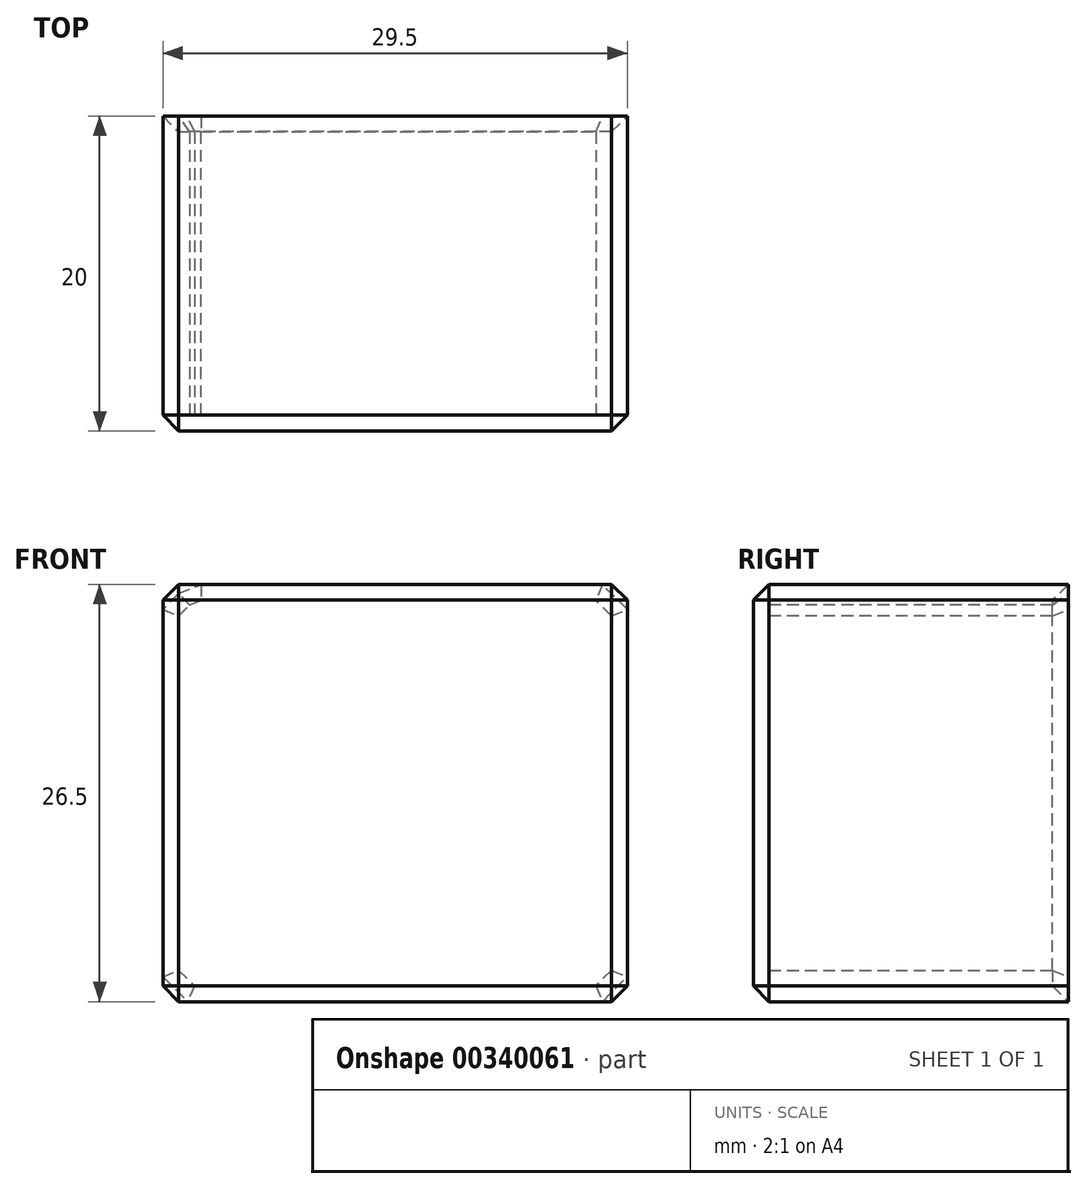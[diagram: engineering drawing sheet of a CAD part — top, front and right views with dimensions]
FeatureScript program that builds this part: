
annotation { "Feature Type Name" : "Feature", "Feature Type Description" : "" }
export const myFeature = defineFeature(function(context is Context, id is Id, definition is map)
    precondition{}
    {
        {
            var Q0;
            Q0=qCreatedBy(makeId("Front.planeOp"),FACE);
            var sketch = newSketch(context, id + "F0", { "sketchPlane" : qUnion([Q0])});
            skLineSegment(sketch, "E0.bottom", {"start": v(0, 0) * mm, "end": v(27.5, 0) * mm});
            skLineSegment(sketch, "E0.top", {"start": v(0, -24.5) * mm, "end": v(27.5, -24.5) * mm});
            skLineSegment(sketch, "E0.left", {"start": v(0, 0) * mm, "end": v(0, -24.5) * mm});
            skLineSegment(sketch, "E0.right", {"start": v(27.5, 0) * mm, "end": v(27.5, -24.5) * mm});
            skLineSegment(sketch, "E1", {"start": v(-1, 1) * mm, "end": v(-1, -25.5) * mm});
            skLineSegment(sketch, "E2", {"start": v(-1, 1) * mm, "end": v(28.5, 1) * mm});
            skLineSegment(sketch, "E3", {"start": v(28.5, 1) * mm, "end": v(28.5, -25.5) * mm});
            skLineSegment(sketch, "E4", {"start": v(28.5, -25.5) * mm, "end": v(-1, -25.5) * mm});
            skSolve(sketch);
        }
        {
            var Q0;
            Q0=makeQuery(id+"F0.imprint","IMPRINT",FACE,{"disambiguationData":[TD([[makeQuery(id+"F0.imprint","IMPRINT",EDGE,{"derivedFrom":sQuery(id+"F0.wireOp",EDGE,"E0.bottom")}),1.0]])]});
            extrude(context, id + "F1", {"entities" : qUnion([Q0]), "oppositeDirection" : true, "depth" : 20 * mm});
        }
        {
            var Q0;
            Q0=makeQuery(id+"F0.imprint","IMPRINT",FACE,{"disambiguationData":[TD([[makeQuery(id+"F0.imprint","IMPRINT",EDGE,{"derivedFrom":sQuery(id+"F0.wireOp",EDGE,"E0.bottom")}),-1.0]])]});
            var Q1;
            Q1=makeQuery(id+"F0.imprint","IMPRINT",FACE,{"disambiguationData":[TD([[makeQuery(id+"F0.imprint","IMPRINT",EDGE,{"derivedFrom":sQuery(id+"F0.wireOp",EDGE,"E0.bottom")}),1.0]])]});
            extrude(context, id + "F2", {"entities" : qUnion([Q0, Q1]), "operationType" : NewBodyOperationType.ADD, "oppositeDirection" : true, "depth" : 1 * mm});
        }
        {
            var Q0;
            Q0=makeQuery(id+"F1.opExtrude","SWEPT_EDGE",EDGE,{"disambiguationData":[OSD([sQuery(id+"F0.wireOp",EDGE,"E0.bottom"),sQuery(id+"F0.wireOp",EDGE,"E0.left")])]});
            var Q1;
            Q1=makeQuery(id+"F1.opExtrude","CAP_EDGE",EDGE,{"disambiguationData":[OSD([sQuery(id+"F0.wireOp",EDGE,"E0.bottom")])],"isStart":true});
            var Q2;
            Q2=makeQuery(id+"F1.opExtrude","CAP_EDGE",EDGE,{"disambiguationData":[OSD([sQuery(id+"F0.wireOp",EDGE,"E0.left")])],"isStart":true});
            var Q3;
            Q3=makeQuery(id+"F1.opExtrude","SWEPT_EDGE",EDGE,{"disambiguationData":[OSD([sQuery(id+"F0.wireOp",EDGE,"E0.top"),sQuery(id+"F0.wireOp",EDGE,"E0.left")])]});
            var Q4;
            Q4=makeQuery(id+"F1.opExtrude","CAP_EDGE",EDGE,{"disambiguationData":[OSD([sQuery(id+"F0.wireOp",EDGE,"E0.top")])],"isStart":true});
            var Q5;
            Q5=makeQuery(id+"F1.opExtrude","SWEPT_EDGE",EDGE,{"disambiguationData":[OSD([sQuery(id+"F0.wireOp",EDGE,"E0.top"),sQuery(id+"F0.wireOp",EDGE,"E0.right")])]});
            var Q6;
            Q6=makeQuery(id+"F1.opExtrude","CAP_EDGE",EDGE,{"disambiguationData":[OSD([sQuery(id+"F0.wireOp",EDGE,"E0.right")])],"isStart":true});
            var Q7;
            Q7=makeQuery(id+"F1.opExtrude","SWEPT_EDGE",EDGE,{"disambiguationData":[OSD([sQuery(id+"F0.wireOp",EDGE,"E0.bottom"),sQuery(id+"F0.wireOp",EDGE,"E0.right")])]});
            var Q8;
            {var subQ0=sQuery(id+"F0.wireOp",EDGE,"E2");var subQ1=sQuery(id+"F0.wireOp",EDGE,"E1");Q8=makeQuery(id+"F2.boolean.opBoolean","MERGE",EDGE,{"derivedFrom":[makeQuery(id+"F1.opExtrude","SWEPT_EDGE",EDGE,{"disambiguationData":[OSD([subQ1,subQ0])]}),makeQuery(id+"F2.opExtrude","SWEPT_EDGE",EDGE,{"disambiguationData":[OSD([subQ1,subQ0])]})]});}
            var Q9;
            {var subQ0=sQuery(id+"F0.wireOp",EDGE,"E4");var subQ1=sQuery(id+"F0.wireOp",EDGE,"E1");Q9=makeQuery(id+"F2.boolean.opBoolean","MERGE",EDGE,{"derivedFrom":[makeQuery(id+"F1.opExtrude","SWEPT_EDGE",EDGE,{"disambiguationData":[OSD([subQ1,subQ0])]}),makeQuery(id+"F2.opExtrude","SWEPT_EDGE",EDGE,{"disambiguationData":[OSD([subQ1,subQ0])]})]});}
            var Q10;
            Q10=makeQuery(id+"F2.opExtrude","CAP_EDGE",EDGE,{"disambiguationData":[OSD([sQuery(id+"F0.wireOp",EDGE,"E1")])],"isStart":false});
            var Q11;
            {var subQ0=sQuery(id+"F0.wireOp",EDGE,"E4");var subQ1=sQuery(id+"F0.wireOp",EDGE,"E3");Q11=makeQuery(id+"F2.boolean.opBoolean","MERGE",EDGE,{"derivedFrom":[makeQuery(id+"F1.opExtrude","SWEPT_EDGE",EDGE,{"disambiguationData":[OSD([subQ1,subQ0])]}),makeQuery(id+"F2.opExtrude","SWEPT_EDGE",EDGE,{"disambiguationData":[OSD([subQ1,subQ0])]})]});}
            var Q12;
            {var subQ0=sQuery(id+"F0.wireOp",EDGE,"E3");var subQ1=sQuery(id+"F0.wireOp",EDGE,"E2");Q12=makeQuery(id+"F2.boolean.opBoolean","MERGE",EDGE,{"derivedFrom":[makeQuery(id+"F1.opExtrude","SWEPT_EDGE",EDGE,{"disambiguationData":[OSD([subQ1,subQ0])]}),makeQuery(id+"F2.opExtrude","SWEPT_EDGE",EDGE,{"disambiguationData":[OSD([subQ1,subQ0])]})]});}
            var Q13;
            Q13=makeQuery(id+"F2.opExtrude","CAP_EDGE",EDGE,{"disambiguationData":[OSD([sQuery(id+"F0.wireOp",EDGE,"E4")])],"isStart":false});
            var Q14;
            Q14=makeQuery(id+"F2.opExtrude","CAP_EDGE",EDGE,{"disambiguationData":[OSD([sQuery(id+"F0.wireOp",EDGE,"E3")])],"isStart":false});
            var Q15;
            Q15=makeQuery(id+"F2.opExtrude","CAP_EDGE",EDGE,{"disambiguationData":[OSD([sQuery(id+"F0.wireOp",EDGE,"E2")])],"isStart":false});
            var Q16;
            Q16=makeQuery(id+"F1.opExtrude","CAP_EDGE",EDGE,{"disambiguationData":[OSD([sQuery(id+"F0.wireOp",EDGE,"E1")])],"isStart":true});
            var Q17;
            Q17=makeQuery(id+"F1.opExtrude","CAP_EDGE",EDGE,{"disambiguationData":[OSD([sQuery(id+"F0.wireOp",EDGE,"E2")])],"isStart":true});
            var Q18;
            Q18=makeQuery(id+"F1.opExtrude","CAP_EDGE",EDGE,{"disambiguationData":[OSD([sQuery(id+"F0.wireOp",EDGE,"E3")])],"isStart":true});
            var Q19;
            Q19=makeQuery(id+"F1.opExtrude","CAP_EDGE",EDGE,{"disambiguationData":[OSD([sQuery(id+"F0.wireOp",EDGE,"E4")])],"isStart":true});
            chamfer(context, id + "F3", {"entities" : qUnion([Q0, Q1, Q2, Q3, Q4, Q5, Q6, Q7, Q8, Q9, Q10, Q11, Q12, Q13, Q14, Q15, Q16, Q17, Q18, Q19]), "width" : 1 * mm, "tangentPropagation" : true});
        }
        {
            var Q0;
            Q0=makeQuery(id+"F1.opExtrude","CAP_EDGE",EDGE,{"disambiguationData":[OSD([sQuery(id+"F0.wireOp",EDGE,"E0.right")])],"isStart":false});
            var Q1;
            {var subQ0=sQuery(id+"F0.wireOp",EDGE,"E0.right");var subQ1=sQuery(id+"F0.wireOp",EDGE,"E0.bottom");Q1=makeQuery(id+"F3.opChamfer","BLEND_EDGE",EDGE,{"blendedFrom":[makeQuery(id+"F1.opExtrude","SWEPT_EDGE",EDGE,{"disambiguationData":[OSD([subQ1,subQ0])]}),makeQuery(id+"F1.opExtrude","CAP_FACE",FACE,{"disambiguationData":[OSD([subQ1,sQuery(id+"F0.wireOp",EDGE,"E0.top"),sQuery(id+"F0.wireOp",EDGE,"E0.left"),subQ0,sQuery(id+"F0.wireOp",EDGE,"E1"),sQuery(id+"F0.wireOp",EDGE,"E2"),sQuery(id+"F0.wireOp",EDGE,"E3"),sQuery(id+"F0.wireOp",EDGE,"E4")])],"isStart":false})],"blendedInto":[makeQuery(id+"F1.opExtrude","CAP_FACE",FACE,{"disambiguationData":[OSD([subQ1,sQuery(id+"F0.wireOp",EDGE,"E0.top"),sQuery(id+"F0.wireOp",EDGE,"E0.left"),subQ0,sQuery(id+"F0.wireOp",EDGE,"E1"),sQuery(id+"F0.wireOp",EDGE,"E2"),sQuery(id+"F0.wireOp",EDGE,"E3"),sQuery(id+"F0.wireOp",EDGE,"E4")])],"isStart":false})]});}
            var Q2;
            Q2=makeQuery(id+"F1.opExtrude","CAP_EDGE",EDGE,{"disambiguationData":[OSD([sQuery(id+"F0.wireOp",EDGE,"E0.bottom")])],"isStart":false});
            var Q3;
            {var subQ0=sQuery(id+"F0.wireOp",EDGE,"E0.bottom");Q3=makeQuery(id+"F3.opChamfer","BLEND_EDGE",EDGE,{"blendedFrom":[makeQuery(id+"F1.opExtrude","SWEPT_EDGE",EDGE,{"disambiguationData":[OSD([subQ0,sQuery(id+"F0.wireOp",EDGE,"E0.left")])]}),makeQuery(id+"F1.opExtrude","SWEPT_FACE",FACE,{"disambiguationData":[OSD([subQ0])]})],"blendedInto":[makeQuery(id+"F1.opExtrude","SWEPT_FACE",FACE,{"disambiguationData":[OSD([subQ0])]})]});}
            var Q4;
            Q4=makeQuery(id+"F1.opExtrude","CAP_EDGE",EDGE,{"disambiguationData":[OSD([sQuery(id+"F0.wireOp",EDGE,"E0.left")])],"isStart":false});
            var Q5;
            {var subQ0=sQuery(id+"F0.wireOp",EDGE,"E0.left");var subQ1=sQuery(id+"F0.wireOp",EDGE,"E0.top");Q5=makeQuery(id+"F3.opChamfer","BLEND_EDGE",EDGE,{"blendedFrom":[makeQuery(id+"F1.opExtrude","SWEPT_EDGE",EDGE,{"disambiguationData":[OSD([subQ1,subQ0])]}),makeQuery(id+"F1.opExtrude","CAP_FACE",FACE,{"disambiguationData":[OSD([sQuery(id+"F0.wireOp",EDGE,"E0.bottom"),subQ1,subQ0,sQuery(id+"F0.wireOp",EDGE,"E0.right"),sQuery(id+"F0.wireOp",EDGE,"E1"),sQuery(id+"F0.wireOp",EDGE,"E2"),sQuery(id+"F0.wireOp",EDGE,"E3"),sQuery(id+"F0.wireOp",EDGE,"E4")])],"isStart":false})],"blendedInto":[makeQuery(id+"F1.opExtrude","CAP_FACE",FACE,{"disambiguationData":[OSD([sQuery(id+"F0.wireOp",EDGE,"E0.bottom"),subQ1,subQ0,sQuery(id+"F0.wireOp",EDGE,"E0.right"),sQuery(id+"F0.wireOp",EDGE,"E1"),sQuery(id+"F0.wireOp",EDGE,"E2"),sQuery(id+"F0.wireOp",EDGE,"E3"),sQuery(id+"F0.wireOp",EDGE,"E4")])],"isStart":false})]});}
            var Q6;
            Q6=makeQuery(id+"F1.opExtrude","CAP_EDGE",EDGE,{"disambiguationData":[OSD([sQuery(id+"F0.wireOp",EDGE,"E0.top")])],"isStart":false});
            var Q7;
            {var subQ0=sQuery(id+"F0.wireOp",EDGE,"E0.right");var subQ1=sQuery(id+"F0.wireOp",EDGE,"E0.top");Q7=makeQuery(id+"F3.opChamfer","BLEND_EDGE",EDGE,{"blendedFrom":[makeQuery(id+"F1.opExtrude","SWEPT_EDGE",EDGE,{"disambiguationData":[OSD([subQ1,subQ0])]}),makeQuery(id+"F1.opExtrude","CAP_FACE",FACE,{"disambiguationData":[OSD([sQuery(id+"F0.wireOp",EDGE,"E0.bottom"),subQ1,sQuery(id+"F0.wireOp",EDGE,"E0.left"),subQ0,sQuery(id+"F0.wireOp",EDGE,"E1"),sQuery(id+"F0.wireOp",EDGE,"E2"),sQuery(id+"F0.wireOp",EDGE,"E3"),sQuery(id+"F0.wireOp",EDGE,"E4")])],"isStart":false})],"blendedInto":[makeQuery(id+"F1.opExtrude","CAP_FACE",FACE,{"disambiguationData":[OSD([sQuery(id+"F0.wireOp",EDGE,"E0.bottom"),subQ1,sQuery(id+"F0.wireOp",EDGE,"E0.left"),subQ0,sQuery(id+"F0.wireOp",EDGE,"E1"),sQuery(id+"F0.wireOp",EDGE,"E2"),sQuery(id+"F0.wireOp",EDGE,"E3"),sQuery(id+"F0.wireOp",EDGE,"E4")])],"isStart":false})]});}
            chamfer(context, id + "F4", {"entities" : qUnion([Q0, Q1, Q2, Q3, Q4, Q5, Q6, Q7]), "width" : 1 * mm, "tangentPropagation" : true});
        }
    });
